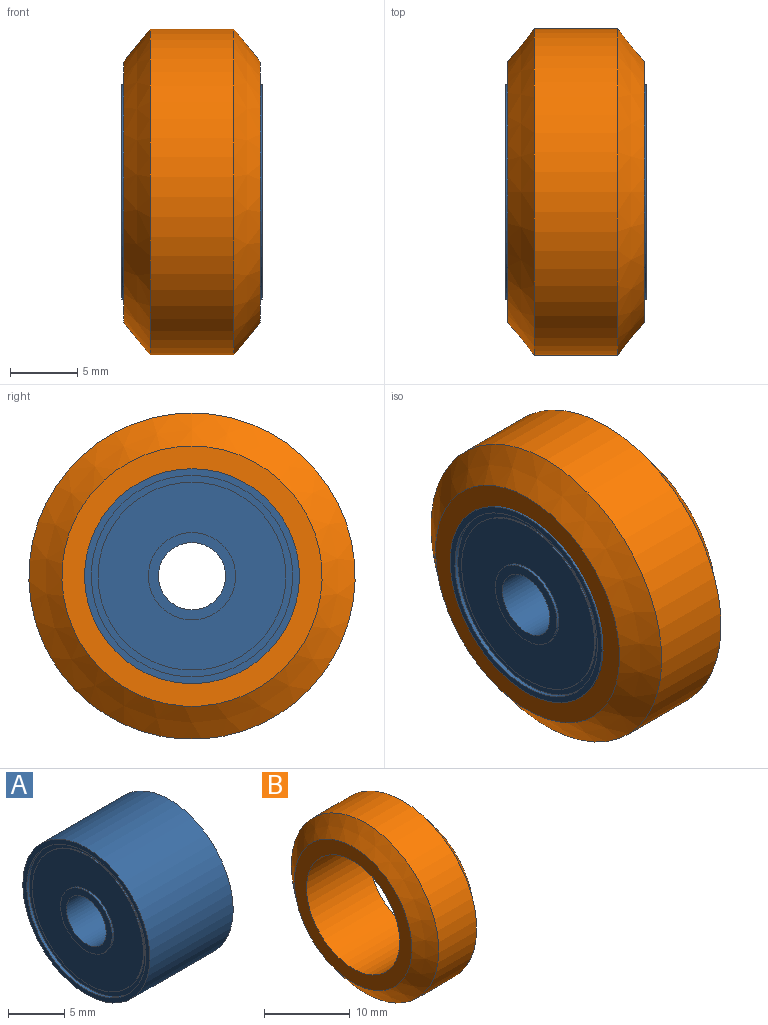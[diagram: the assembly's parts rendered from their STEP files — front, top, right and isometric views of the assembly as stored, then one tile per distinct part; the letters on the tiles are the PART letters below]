
ASSEMBLY  parts=2 mates=2
PART A: 20 faces, bbox 10.5x16x16 mm
  f0: cylinder r=8mm len=16mm, axis (-1,0,0), area 527.8mm2, adj f1,f19
  f1: plane 16x16mm, normal (-1,0,0), area 24.3mm2, adj f0,f2
  f2: cylinder r=7.5mm len=15mm, axis (-1,0,0), area 14.1mm2, adj f1,f3
  f3: plane 15x15mm, normal (-1,0,0), area 22.8mm2, adj f2,f4
  f4: cylinder r=7mm len=14mm, axis (-1,0,0), area 4.4mm2, adj f3,f5
  f5: plane 14x14mm, normal (-1,0,0), area 120.8mm2, adj f4,f6
  f6: cylinder r=3.25mm len=6.5mm, axis (-1,0,0), area 4.1mm2, adj f5,f7
  f7: plane 6.5x6.5mm, normal (-1,0,0), area 13.5mm2, adj f6,f8
  f8: cylinder r=2.5mm len=5mm, axis (-1,0,0), area 78.5mm2, adj f7,f9
  f9: plane 13.8x13.8mm, normal (1,0,0), area 129.9mm2, adj f8,f10
  f10: cylinder r=6.9mm len=13.8mm, axis (-1,0,0), area 21.7mm2, adj f9,f11
  f11: plane 13.8x13.8mm, normal (-1,0,0), area 129.9mm2, adj f10,f12
  f12: cylinder r=2.5mm len=5mm, axis (-1,0,0), area 78.5mm2, adj f11,f13
  f13: plane 6.5x6.5mm, normal (1,0,0), area 13.5mm2, adj f12,f14
  f14: cylinder r=3.25mm len=6.5mm, axis (-1,0,0), area 4.1mm2, adj f13,f15
  f15: plane 14x14mm, normal (1,0,0), area 120.8mm2, adj f14,f16
  f16: cylinder r=7mm len=14mm, axis (-1,0,0), area 4.4mm2, adj f15,f17
  f17: plane 15x15mm, normal (1,0,0), area 22.8mm2, adj f16,f18
  f18: cylinder r=7.5mm len=15mm, axis (-1,0,0), area 14.1mm2, adj f17,f19
  f19: plane 16x16mm, normal (1,0,0), area 24.3mm2, adj f0,f18
PART B: 6 faces, bbox 10.2x24.3x24.3 mm
  f0: plane 19.38x19.38mm, normal (-1,0,0), area 109.2mm2, adj f1,f5
  f1: cylinder r=7.69mm len=15.38mm, axis (-1,0,0), area 492.8mm2, adj f0,f2
  f2: plane 19.38x19.38mm, normal (1,0,0), area 109.2mm2, adj f1,f3
  f3: cone r=9.69mm half-angle=51.2deg, axis (-1,0,0), area 216.5mm2, adj f2,f4
  f4: cylinder r=12.15mm len=24.3mm, axis (-1,0,0), area 477.1mm2, adj f3,f5
  f5: cone r=9.69mm half-angle=51.2deg, axis (1,0,0), area 216.5mm2, adj f0,f4
PLACE A t=(5.35,-15.5,6.49)mm
PLACE B t=(5.35,-15.5,6.49)mm
MATE cylindrical A.f0 <-> B.f1  axis (-1,0,0) through (5.35,-15.5,6.49)mm
MATE planar A.f0 <-> B.f1  axis (-1,0,0) through (5.35,-15.5,6.49)mm
